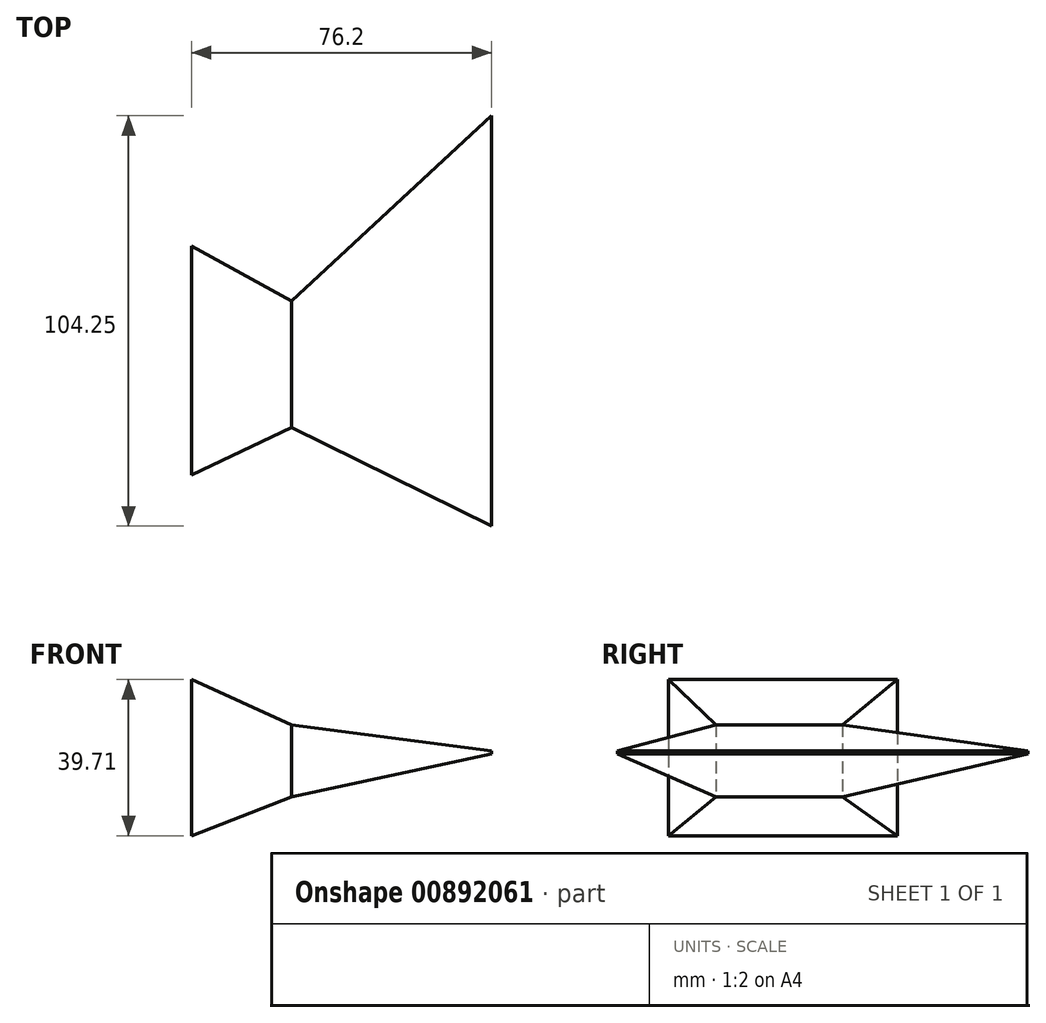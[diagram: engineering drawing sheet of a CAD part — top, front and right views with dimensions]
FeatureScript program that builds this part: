
annotation { "Feature Type Name" : "Feature", "Feature Type Description" : "" }
export const myFeature = defineFeature(function(context is Context, id is Id, definition is map)
    precondition{}
    {
        {
            var Q0;
            Q0=qCreatedBy(makeId("Right.planeOp"),FACE);
            var sketch = newSketch(context, id + "F0", { "sketchPlane" : qUnion([Q0])});
            skLineSegment(sketch, "E0.bottom", {"start": v(-30.8, 22.1) * mm, "end": v(27.36, 22.1) * mm});
            skLineSegment(sketch, "E0.top", {"start": v(-30.8, -17.6) * mm, "end": v(27.36, -17.6) * mm});
            skLineSegment(sketch, "E0.left", {"start": v(-30.8, 22.1) * mm, "end": v(-30.8, -17.6) * mm});
            skLineSegment(sketch, "E0.right", {"start": v(27.36, 22.1) * mm, "end": v(27.36, -17.6) * mm});
            skSolve(sketch);
        }
        {
            var Q0;
            Q0=makeQuery(id+"F0.imprint","IMPRINT",FACE,{"disambiguationData":[TD([[makeQuery(id+"F0.imprint","IMPRINT",EDGE,{"derivedFrom":sQuery(id+"F0.wireOp",EDGE,"E0.bottom")}),-1.0]])]});
            cPlane(context, id + "F1", {"entities" : qUnion([Q0]), "cplaneType" : CPlaneType.OFFSET, "offset" : 25.4 * mm, "width" : 152.4 * mm, "height" : 152.4 * mm});
        }
        {
            var Q0;
            Q0=qCreatedBy(id+"F1.planeOp",FACE);
            var sketch = newSketch(context, id + "F2", { "sketchPlane" : qUnion([Q0])});
            skLineSegment(sketch, "E1.bottom", {"start": v(-18.78, 10.52) * mm, "end": v(13.41, 10.52) * mm});
            skLineSegment(sketch, "E1.top", {"start": v(-18.78, -7.73) * mm, "end": v(13.41, -7.73) * mm});
            skLineSegment(sketch, "E1.left", {"start": v(-18.78, 10.52) * mm, "end": v(-18.78, -7.73) * mm});
            skLineSegment(sketch, "E1.right", {"start": v(13.41, 10.52) * mm, "end": v(13.41, -7.73) * mm});
            skSolve(sketch);
        }
        {
            var Q0;
            Q0=makeQuery(id+"F0.imprint","IMPRINT",FACE,{"disambiguationData":[TD([[makeQuery(id+"F0.imprint","IMPRINT",EDGE,{"derivedFrom":sQuery(id+"F0.wireOp",EDGE,"E0.bottom")}),-1.0]])]});
            var Q1;
            Q1=makeQuery(id+"F2.imprint","IMPRINT",FACE,{"disambiguationData":[TD([[makeQuery(id+"F2.imprint","IMPRINT",EDGE,{"derivedFrom":sQuery(id+"F2.wireOp",EDGE,"E1.bottom")}),-1.0]])]});
            loft(context, id + "F3", {"sheetProfilesArray" : [{ "sheetProfileEntities" : qUnion([Q0]) }, { "sheetProfileEntities" : qUnion([Q1]) }]});
        }
        {
            var Q0;
            Q0=makeQuery(id+"F3.opLoft","CAP_FACE",FACE,{"disambiguationData":[OSD([makeQuery(id+"F2.imprint","IMPRINT",FACE,{"disambiguationData":[TD([[makeQuery(id+"F2.imprint","IMPRINT",EDGE,{"derivedFrom":sQuery(id+"F2.wireOp",EDGE,"E1.bottom")}),-1.0]])]})])],"isStart":true});
            cPlane(context, id + "F4", {"entities" : qUnion([Q0]), "cplaneType" : CPlaneType.OFFSET, "offset" : 50.8 * mm, "width" : 152.4 * mm, "height" : 152.4 * mm});
        }
        {
            var Q0;
            Q0=qCreatedBy(id+"F4.planeOp",FACE);
            var sketch = newSketch(context, id + "F5", { "sketchPlane" : qUnion([Q0])});
            skLineSegment(sketch, "E2.bottom", {"start": v(-43.78, 3.92) * mm, "end": v(60.47, 3.92) * mm});
            skLineSegment(sketch, "E2.top", {"start": v(-43.78, 3.23) * mm, "end": v(60.47, 3.23) * mm});
            skLineSegment(sketch, "E2.left", {"start": v(-43.78, 3.92) * mm, "end": v(-43.78, 3.23) * mm});
            skLineSegment(sketch, "E2.right", {"start": v(60.47, 3.92) * mm, "end": v(60.47, 3.23) * mm});
            skSolve(sketch);
        }
        {
            var Q1;
            Q1=makeQuery(id+"F3.opLoft","CAP_FACE",FACE,{"disambiguationData":[OSD([makeQuery(id+"F2.imprint","IMPRINT",FACE,{"disambiguationData":[TD([[makeQuery(id+"F2.imprint","IMPRINT",EDGE,{"derivedFrom":sQuery(id+"F2.wireOp",EDGE,"E1.bottom")}),-1.0]])]})])],"isStart":true});
            var Q2;
            Q2=makeQuery(id+"F5.imprint","IMPRINT",FACE,{"disambiguationData":[TD([[makeQuery(id+"F5.imprint","IMPRINT",EDGE,{"derivedFrom":sQuery(id+"F5.wireOp",EDGE,"E2.bottom")}),-1.0]])]});
            loft(context, id + "F6", {"operationType" : NewBodyOperationType.ADD, "sheetProfilesArray" : [{ "sheetProfileEntities" : qUnion([Q1]) }, { "sheetProfileEntities" : qUnion([Q2]) }]});
        }
    });
